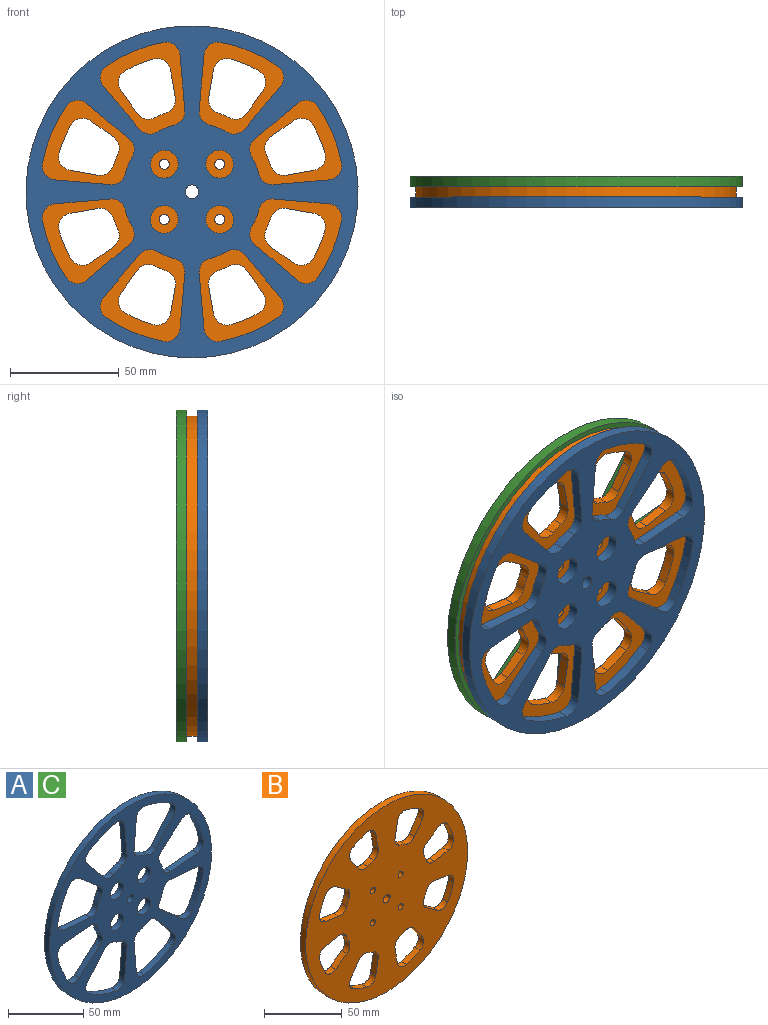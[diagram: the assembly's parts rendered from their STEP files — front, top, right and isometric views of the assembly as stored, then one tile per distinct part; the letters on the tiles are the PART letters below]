
ASSEMBLY  parts=3 mates=2
PART A: 72 faces, bbox 152.4x4.8x152.4 mm
  f0: cylinder r=69.85mm len=26.31mm, axis (0,1,0), area 136.6mm2, adj f1,f61,f70,f71
  f1: cylinder r=6.35mm len=9.33mm, axis (0,1,0), area 50.5mm2, adj f0,f2,f70,f71
  f2: plane 19.62x16.46mm, normal (-0.77,0,0.64), area 122mm2, adj f1,f3,f70,f71
  f3: cylinder r=6.35mm len=8.08mm, axis (0,1,0), area 42.4mm2, adj f2,f4,f70,f71
  f4: cylinder r=31.75mm len=8.07mm, axis (0,1,0), area 41.7mm2, adj f3,f5,f70,f71
  f5: cylinder r=6.35mm len=6.7mm, axis (0,1,0), area 42.4mm2, adj f4,f6,f70,f71
  f6: plane 25.52x4.76mm, normal (1,0,-0.09), area 122mm2, adj f5,f61,f70,f71
  f7: cylinder r=69.85mm len=26.31mm, axis (0,1,0), area 136.6mm2, adj f8,f62,f70,f71
  f8: cylinder r=6.35mm len=7.51mm, axis (0,1,0), area 50.5mm2, adj f7,f9,f70,f71
  f9: plane 25.52x4.76mm, normal (-1,0,-0.09), area 122mm2, adj f8,f10,f70,f71
  f10: cylinder r=6.35mm len=6.7mm, axis (0,1,0), area 42.4mm2, adj f9,f11,f70,f71
  f11: cylinder r=31.75mm len=8.07mm, axis (0,1,0), area 41.7mm2, adj f10,f12,f70,f71
  f12: cylinder r=6.35mm len=8.08mm, axis (0,1,0), area 42.4mm2, adj f11,f13,f70,f71
  f13: plane 19.62x16.46mm, normal (0.77,0,0.64), area 122mm2, adj f12,f62,f70,f71
  f14: cylinder r=69.85mm len=26.31mm, axis (0,1,0), area 136.6mm2, adj f15,f63,f70,f71
  f15: cylinder r=6.35mm len=9.33mm, axis (0,1,0), area 50.5mm2, adj f14,f16,f70,f71
  f16: plane 19.62x16.46mm, normal (-0.64,0,-0.77), area 122mm2, adj f15,f17,f70,f71
  f17: cylinder r=6.35mm len=8.08mm, axis (0,1,0), area 42.4mm2, adj f16,f18,f70,f71
  f18: cylinder r=31.75mm len=8.07mm, axis (0,1,0), area 41.7mm2, adj f17,f19,f70,f71
  f19: cylinder r=6.35mm len=6.7mm, axis (0,1,0), area 42.4mm2, adj f18,f20,f70,f71
  f20: plane 25.52x4.76mm, normal (0.09,0,1), area 122mm2, adj f19,f63,f70,f71
  f21: cylinder r=69.85mm len=26.31mm, axis (0,1,0), area 136.6mm2, adj f22,f64,f70,f71
  f22: cylinder r=6.35mm len=7.51mm, axis (0,1,0), area 50.5mm2, adj f21,f23,f70,f71
  f23: plane 25.52x4.76mm, normal (0.09,0,-1), area 122mm2, adj f22,f24,f70,f71
  f24: cylinder r=6.35mm len=6.7mm, axis (0,1,0), area 42.4mm2, adj f23,f25,f70,f71
  f25: cylinder r=31.75mm len=8.07mm, axis (0,1,0), area 41.7mm2, adj f24,f26,f70,f71
  f26: cylinder r=6.35mm len=8.08mm, axis (0,1,0), area 42.4mm2, adj f25,f27,f70,f71
  f27: plane 19.62x16.46mm, normal (-0.64,0,0.77), area 122mm2, adj f26,f64,f70,f71
  f28: cylinder r=69.85mm len=26.31mm, axis (0,1,0), area 136.6mm2, adj f29,f65,f70,f71
  f29: cylinder r=6.35mm len=9.33mm, axis (0,1,0), area 50.5mm2, adj f28,f30,f70,f71
  f30: plane 19.62x16.46mm, normal (0.77,0,-0.64), area 122mm2, adj f29,f31,f70,f71
  f31: cylinder r=6.35mm len=8.08mm, axis (0,1,0), area 42.4mm2, adj f30,f32,f70,f71
  f32: cylinder r=31.75mm len=8.07mm, axis (0,1,0), area 41.7mm2, adj f31,f33,f70,f71
  f33: cylinder r=6.35mm len=6.7mm, axis (0,1,0), area 42.4mm2, adj f32,f34,f70,f71
  f34: plane 25.52x4.76mm, normal (-1,0,0.09), area 122mm2, adj f33,f65,f70,f71
  f35: cylinder r=69.85mm len=26.31mm, axis (0,1,0), area 136.6mm2, adj f36,f66,f70,f71
  f36: cylinder r=6.35mm len=7.51mm, axis (0,1,0), area 50.5mm2, adj f35,f37,f70,f71
  f37: plane 25.52x4.76mm, normal (1,0,0.09), area 122mm2, adj f36,f38,f70,f71
  f38: cylinder r=6.35mm len=6.7mm, axis (0,1,0), area 42.4mm2, adj f37,f39,f70,f71
  f39: cylinder r=31.75mm len=8.07mm, axis (0,1,0), area 41.7mm2, adj f38,f40,f70,f71
  f40: cylinder r=6.35mm len=8.08mm, axis (0,1,0), area 42.4mm2, adj f39,f41,f70,f71
  f41: plane 19.62x16.46mm, normal (-0.77,0,-0.64), area 122mm2, adj f40,f66,f70,f71
  f42: cylinder r=69.85mm len=26.31mm, axis (0,1,0), area 136.6mm2, adj f43,f67,f70,f71
  f43: cylinder r=6.35mm len=9.33mm, axis (0,1,0), area 50.5mm2, adj f42,f44,f70,f71
  f44: plane 19.62x16.46mm, normal (0.64,0,0.77), area 122mm2, adj f43,f45,f70,f71
  f45: cylinder r=6.35mm len=8.08mm, axis (0,1,0), area 42.4mm2, adj f44,f46,f70,f71
  f46: cylinder r=31.75mm len=8.07mm, axis (0,1,0), area 41.7mm2, adj f45,f47,f70,f71
  f47: cylinder r=6.35mm len=6.7mm, axis (0,1,0), area 42.4mm2, adj f46,f48,f70,f71
  f48: plane 25.52x4.76mm, normal (-0.09,0,-1), area 122mm2, adj f47,f67,f70,f71
  f49: cylinder r=69.85mm len=26.31mm, axis (0,1,0), area 136.6mm2, adj f50,f68,f70,f71
  f50: cylinder r=6.35mm len=7.51mm, axis (0,1,0), area 50.5mm2, adj f49,f51,f70,f71
  f51: plane 25.52x4.76mm, normal (-0.09,0,1), area 122mm2, adj f50,f52,f70,f71
  f52: cylinder r=6.35mm len=6.7mm, axis (0,1,0), area 42.4mm2, adj f51,f53,f70,f71
  f53: cylinder r=31.75mm len=8.07mm, axis (0,1,0), area 41.7mm2, adj f52,f54,f70,f71
  f54: cylinder r=6.35mm len=8.08mm, axis (0,1,0), area 42.4mm2, adj f53,f55,f70,f71
  f55: plane 19.62x16.46mm, normal (0.64,0,-0.77), area 122mm2, adj f54,f68,f70,f71
  f56: cylinder r=6.35mm len=12.7mm, axis (0,1,0), area 190mm2, adj f70,f71
  f57: cylinder r=6.35mm len=12.7mm, axis (0,1,0), area 190mm2, adj f70,f71
  f58: cylinder r=6.35mm len=12.7mm, axis (0,1,0), area 190mm2, adj f70,f71
  f59: cylinder r=6.35mm len=12.7mm, axis (0,1,0), area 190mm2, adj f70,f71
  f60: cylinder r=76.2mm len=152.4mm, axis (0,1,0), area 2280.2mm2, adj f70,f71
  f61: cylinder r=6.35mm len=7.51mm, axis (0,1,0), area 50.5mm2, adj f0,f6,f70,f71
  f62: cylinder r=6.35mm len=9.33mm, axis (0,1,0), area 50.5mm2, adj f7,f13,f70,f71
  f63: cylinder r=6.35mm len=7.51mm, axis (0,1,0), area 50.5mm2, adj f14,f20,f70,f71
  f64: cylinder r=6.35mm len=9.33mm, axis (0,1,0), area 50.5mm2, adj f21,f27,f70,f71
  f65: cylinder r=6.35mm len=7.51mm, axis (0,1,0), area 50.5mm2, adj f28,f34,f70,f71
  f66: cylinder r=6.35mm len=9.33mm, axis (0,1,0), area 50.5mm2, adj f35,f41,f70,f71
  f67: cylinder r=6.35mm len=7.51mm, axis (0,1,0), area 50.5mm2, adj f42,f48,f70,f71
  f68: cylinder r=6.35mm len=9.33mm, axis (0,1,0), area 50.5mm2, adj f49,f55,f70,f71
  f69: cylinder r=3.17mm len=6.35mm, axis (0,1,0), area 95mm2, adj f70,f71
  f70: plane 152.4x152.4mm, normal (0,-1,0), area 8511mm2, adj f0,f1,f2,f3,f4,f5,f6,f7
  f71: plane 152.4x152.4mm, normal (0,1,0), area 8511mm2, adj f0,f1,f2,f3,f4,f5,f6,f7
PART B: 72 faces, bbox 147.3x4.8x147.3 mm
  f0: cylinder r=38.1mm len=5.26mm, axis (0,1,0), area 27.2mm2, adj f1,f56,f70,f71
  f1: cylinder r=6.35mm len=8.06mm, axis (0,1,0), area 43.2mm2, adj f0,f2,f70,f71
  f2: plane 10.49x7.34mm, normal (0.57,0,-0.82), area 61mm2, adj f1,f3,f70,f71
  f3: cylinder r=6.35mm len=9.22mm, axis (0,1,0), area 50.9mm2, adj f2,f4,f70,f71
  f4: cylinder r=63.5mm len=12.51mm, axis (0,1,0), area 64.6mm2, adj f3,f5,f70,f71
  f5: cylinder r=6.35mm len=8.04mm, axis (0,1,0), area 50.9mm2, adj f4,f6,f70,f71
  f6: plane 12.61x4.76mm, normal (-0.17,0,0.98), area 61mm2, adj f5,f56,f70,f71
  f7: cylinder r=6.35mm len=8.06mm, axis (0,1,0), area 43.2mm2, adj f8,f62,f70,f71
  f8: cylinder r=38.1mm len=5.26mm, axis (0,1,0), area 27.2mm2, adj f7,f9,f70,f71
  f9: cylinder r=6.35mm len=7.13mm, axis (0,1,0), area 43.2mm2, adj f8,f10,f70,f71
  f10: plane 12.61x4.76mm, normal (-0.17,0,-0.98), area 61mm2, adj f9,f11,f70,f71
  f11: cylinder r=6.35mm len=8.04mm, axis (0,1,0), area 50.9mm2, adj f10,f12,f70,f71
  f12: cylinder r=63.5mm len=12.51mm, axis (0,1,0), area 64.6mm2, adj f11,f13,f70,f71
  f13: cylinder r=6.35mm len=9.22mm, axis (0,1,0), area 50.9mm2, adj f12,f62,f70,f71
  f14: cylinder r=6.35mm len=7.13mm, axis (0,1,0), area 43.2mm2, adj f15,f63,f70,f71
  f15: cylinder r=38.1mm len=5.26mm, axis (0,1,0), area 27.2mm2, adj f14,f16,f70,f71
  f16: cylinder r=6.35mm len=8.06mm, axis (0,1,0), area 43.2mm2, adj f15,f17,f70,f71
  f17: plane 10.49x7.34mm, normal (-0.82,0,-0.57), area 61mm2, adj f16,f18,f70,f71
  f18: cylinder r=6.35mm len=9.22mm, axis (0,1,0), area 50.9mm2, adj f17,f19,f70,f71
  f19: cylinder r=63.5mm len=12.51mm, axis (0,1,0), area 64.6mm2, adj f18,f20,f70,f71
  f20: cylinder r=6.35mm len=8.04mm, axis (0,1,0), area 50.9mm2, adj f19,f63,f70,f71
  f21: cylinder r=6.35mm len=8.06mm, axis (0,1,0), area 43.2mm2, adj f22,f64,f70,f71
  f22: cylinder r=38.1mm len=5.26mm, axis (0,1,0), area 27.2mm2, adj f21,f23,f70,f71
  f23: cylinder r=6.35mm len=7.13mm, axis (0,1,0), area 43.2mm2, adj f22,f24,f70,f71
  f24: plane 12.61x4.76mm, normal (-0.98,0,0.17), area 61mm2, adj f23,f25,f70,f71
  f25: cylinder r=6.35mm len=8.04mm, axis (0,1,0), area 50.9mm2, adj f24,f26,f70,f71
  f26: cylinder r=63.5mm len=12.51mm, axis (0,1,0), area 64.6mm2, adj f25,f27,f70,f71
  f27: cylinder r=6.35mm len=9.22mm, axis (0,1,0), area 50.9mm2, adj f26,f64,f70,f71
  f28: cylinder r=6.35mm len=8.06mm, axis (0,1,0), area 43.2mm2, adj f29,f65,f70,f71
  f29: cylinder r=38.1mm len=5.26mm, axis (0,1,0), area 27.2mm2, adj f28,f30,f70,f71
  f30: cylinder r=6.35mm len=7.13mm, axis (0,1,0), area 43.2mm2, adj f29,f31,f70,f71
  f31: plane 12.61x4.76mm, normal (0.98,0,-0.17), area 61mm2, adj f30,f32,f70,f71
  f32: cylinder r=6.35mm len=8.04mm, axis (0,1,0), area 50.9mm2, adj f31,f33,f70,f71
  f33: cylinder r=63.5mm len=12.51mm, axis (0,1,0), area 64.6mm2, adj f32,f34,f70,f71
  f34: cylinder r=6.35mm len=9.22mm, axis (0,1,0), area 50.9mm2, adj f33,f65,f70,f71
  f35: plane 12.61x4.76mm, normal (0.17,0,-0.98), area 61mm2, adj f36,f66,f70,f71
  f36: cylinder r=6.35mm len=7.13mm, axis (0,1,0), area 43.2mm2, adj f35,f37,f70,f71
  f37: cylinder r=38.1mm len=5.26mm, axis (0,1,0), area 27.2mm2, adj f36,f38,f70,f71
  f38: cylinder r=6.35mm len=8.06mm, axis (0,1,0), area 43.2mm2, adj f37,f39,f70,f71
  f39: plane 10.49x7.34mm, normal (-0.57,0,0.82), area 61mm2, adj f38,f40,f70,f71
  f40: cylinder r=6.35mm len=9.22mm, axis (0,1,0), area 50.9mm2, adj f39,f41,f70,f71
  f41: cylinder r=63.5mm len=12.51mm, axis (0,1,0), area 64.6mm2, adj f40,f66,f70,f71
  f42: plane 12.61x4.76mm, normal (0.17,0,0.98), area 61mm2, adj f43,f67,f70,f71
  f43: cylinder r=6.35mm len=8.04mm, axis (0,1,0), area 50.9mm2, adj f42,f44,f70,f71
  f44: cylinder r=63.5mm len=12.51mm, axis (0,1,0), area 64.6mm2, adj f43,f45,f70,f71
  f45: cylinder r=6.35mm len=9.22mm, axis (0,1,0), area 50.9mm2, adj f44,f46,f70,f71
  f46: plane 10.49x7.34mm, normal (-0.57,0,-0.82), area 61mm2, adj f45,f47,f70,f71
  f47: cylinder r=6.35mm len=8.06mm, axis (0,1,0), area 43.2mm2, adj f46,f48,f70,f71
  f48: cylinder r=38.1mm len=5.26mm, axis (0,1,0), area 27.2mm2, adj f47,f67,f70,f71
  f49: plane 10.49x7.34mm, normal (0.82,0,0.57), area 61mm2, adj f50,f68,f70,f71
  f50: cylinder r=6.35mm len=9.22mm, axis (0,1,0), area 50.9mm2, adj f49,f51,f70,f71
  f51: cylinder r=63.5mm len=12.51mm, axis (0,1,0), area 64.6mm2, adj f50,f52,f70,f71
  f52: cylinder r=6.35mm len=8.04mm, axis (0,1,0), area 50.9mm2, adj f51,f53,f70,f71
  f53: plane 12.61x4.76mm, normal (-0.98,0,-0.17), area 61mm2, adj f52,f54,f70,f71
  f54: cylinder r=6.35mm len=7.13mm, axis (0,1,0), area 43.2mm2, adj f53,f55,f70,f71
  f55: cylinder r=38.1mm len=5.26mm, axis (0,1,0), area 27.2mm2, adj f54,f68,f70,f71
  f56: cylinder r=6.35mm len=7.13mm, axis (0,1,0), area 43.2mm2, adj f0,f6,f70,f71
  f57: cylinder r=2.32mm len=4.76mm, axis (0,1,0), area 69.5mm2, adj f70,f71
  f58: cylinder r=2.32mm len=4.76mm, axis (0,1,0), area 69.5mm2, adj f70,f71
  f59: cylinder r=2.32mm len=4.76mm, axis (0,1,0), area 69.5mm2, adj f70,f71
  f60: cylinder r=2.32mm len=4.76mm, axis (0,1,0), area 69.5mm2, adj f70,f71
  f61: cylinder r=3.17mm len=6.35mm, axis (0,1,0), area 95mm2, adj f70,f71
  f62: plane 10.49x7.34mm, normal (0.57,0,0.82), area 61mm2, adj f7,f13,f70,f71
  f63: plane 12.61x4.76mm, normal (0.98,0,0.17), area 61mm2, adj f14,f20,f70,f71
  f64: plane 10.49x7.34mm, normal (0.82,0,-0.57), area 61mm2, adj f21,f27,f70,f71
  f65: plane 10.49x7.34mm, normal (-0.82,0,0.57), area 61mm2, adj f28,f34,f70,f71
  f66: cylinder r=6.35mm len=8.04mm, axis (0,1,0), area 50.9mm2, adj f35,f41,f70,f71
  f67: cylinder r=6.35mm len=7.13mm, axis (0,1,0), area 43.2mm2, adj f42,f48,f70,f71
  f68: cylinder r=6.35mm len=8.06mm, axis (0,1,0), area 43.2mm2, adj f49,f55,f70,f71
  f69: cylinder r=73.66mm len=147.32mm, axis (0,1,0), area 2204.2mm2, adj f70,f71
  f70: plane 147.32x147.32mm, normal (0,-1,0), area 12715.6mm2, adj f0,f1,f2,f3,f4,f5,f6,f7
  f71: plane 147.32x147.32mm, normal (0,1,0), area 12715.6mm2, adj f0,f1,f2,f3,f4,f5,f6,f7
PART C: same geometry as A
PLACE A t=(169.12,128.05,56.32)mm
PLACE B t=(169.12,132.81,56.32)mm
PLACE C t=(169.12,137.57,56.32)mm
MATE fastened B.f69 <-> A.f60  axis (0,-1,0) through (169.12,128.05,56.32)mm
MATE fastened B.f69 <-> C.f60  axis (0,1,0) through (169.12,132.81,56.32)mm
